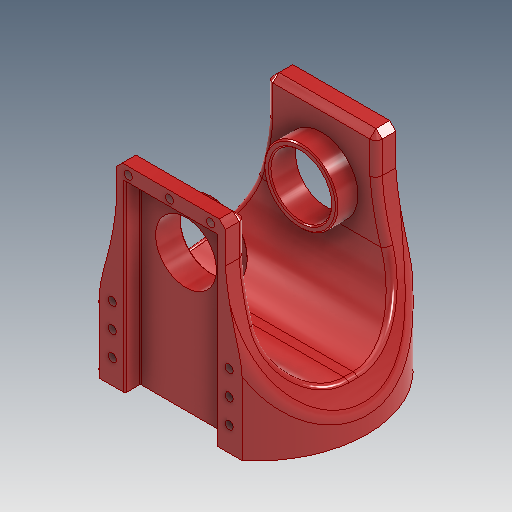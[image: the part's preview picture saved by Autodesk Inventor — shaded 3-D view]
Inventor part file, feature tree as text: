
AUTODESK INVENTOR PART (.ipt)
format: ipt  version: 2020.3 (Build 243373010, 373A)  size: 581,632 bytes
history: native  units: mm
features: sketch x10, extrude x8, fillet x4, mirror x3, chamfer x3, projected_geometry x2, hole x1
ambient origin geometry x8: Origin, YZ Plane, XZ Plane, XY Plane, X Axis, Y Axis, Z Axis, Center Point
bodies: Body1 (feature_tree)
feature tree (31):
  extrude  "Extrusion22"  Depth=10.0mm
  extrude  "Extrusion25"  Depth=325.0mm TaperAngle=0.0deg
  extrude  "Extrusion26"  Depth=60.0mm
  mirror  "Mirror4"
  fillet  "Fillet12"  Radius=182.5mm
  fillet  "Fillet13"  Radius=400.0mm
  extrude  "Extrusion27"  Depth=100.0mm
  sketch  "Sketch57"  dims[d228=182.5mm d229=0.0mm d230=100.0mm]
  extrude  "Extrusion28"  Depth=15.0mm
  extrude  "Extrusion30"  Depth=200.0mm
  hole  "Hole7"  [1 undecoded]
  mirror  "Mirror7"
  chamfer  "Chamfer3"  Distance=140.0mm
  fillet  "Fillet14"  Radius=140.0mm
  fillet  "Fillet15"  Radius=42.5mm
  chamfer  "Chamfer4"  Distance=42.5mm
  extrude  "Extrusion31"  Depth=10.0mm
  extrude  "Extrusion32"  Depth=10.0mm
  mirror  "Mirror8"
  chamfer  "Chamfer5"  Distance=21.0mm
  sketch  "Sketch51"  dims[d25=155.0mm]
  sketch  "Sketch54"  dims[d134=105.0mm d135=10.0mm d148=330.0mm d153=35.0mm d154=85.0mm d155=85.0mm d168=105.0mm d170=105.0mm]
  sketch  "Sketch55"  dims[d207=365.0mm d208=325.0mm d209=0.0mm]
  sketch  "Sketch56"  dims[d210=175.0mm d221=60.0mm d222=65.0mm d223=65.0mm d224=182.5mm d225=0.0mm d226=400.0mm]
  sketch  "Sketch58"  dims[d231=25.0mm d232=15.0mm]
  sketch  "Sketch60"  dims[d233=300.0mm d234=0.0mm d235=200.0mm]
  projected_geometry  "Projected Loop15"
  sketch  "Sketch66"  dims[d236=20.0mm d237=0.0mm d244=0.0mm d245=0.0mm]
  sketch  "Sketch68"  dims[d262=115.0mm]
  sketch  "Sketch69"  dims[d266=51.420479mm d272=140.0mm d273=140.0mm d274=42.5mm d275=42.5mm d279=179.284801mm d280=234.147389mm d281=21.0mm d282=42.170596mm d283=40.0mm d285=40.0mm d286=120.0mm d287=120.0mm d288=21.0mm d289=40.0mm d290=40.0mm d291=135.0mm d292=20.0mm d293=67.5mm d294=25.0mm d295=12.5mm d296=13.376202mm d297=16.5mm d298=3.023mm d299=2.0mm d300=14.3117mm d301=20.0mm d302=20.594885mm d303=2.0mm d304=2.0mm d305=45.0deg d306=2.0mm d307=10.0mm d308=10.0mm d309=2.0mm d310=45.0deg d311=100.125mm d312=225.0mm d313=47.232mm d314=0.0mm d315=10.0mm d316=35.0mm d317=0.0mm d318=2.0mm d319=2.0mm d320=45.0deg d113=0.5mm d114=0.872665mm d115=0.5mm d116=0.872665mm d127=0.5mm d128=0.872665mm d129=0.5mm d130=0.872665mm d264=0.5mm d265=0.872665mm d267=0.872665mm]
  projected_geometry  "Projected Loop17"
note: 1 required parameter value undecoded (feature->parameter linkage not recoverable at this tier; creation-order binding heuristic only, values carry confidence <= 0.55)
